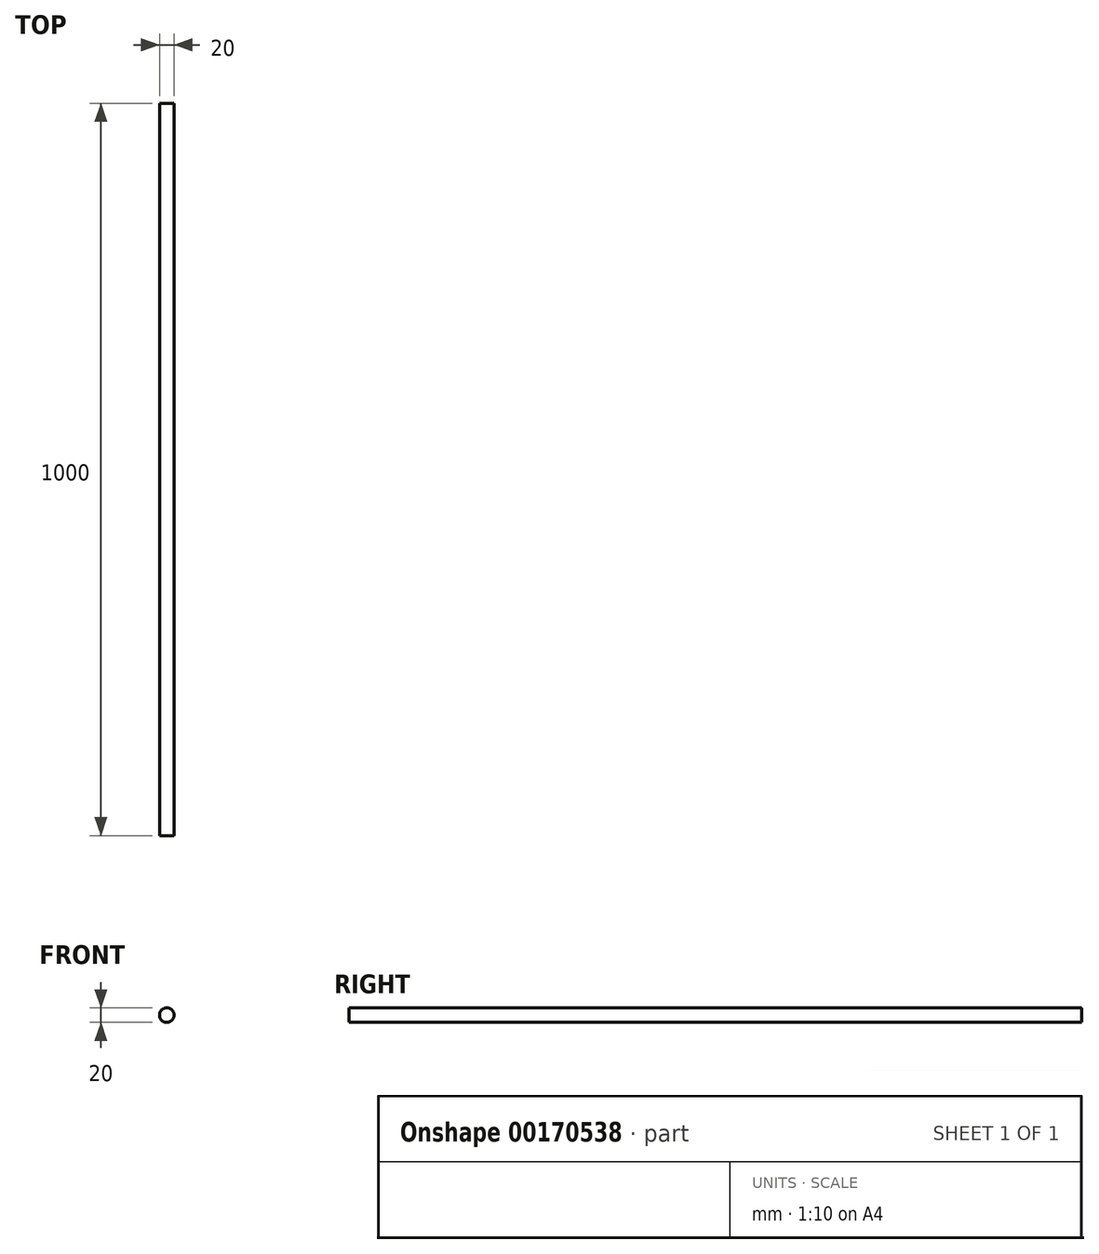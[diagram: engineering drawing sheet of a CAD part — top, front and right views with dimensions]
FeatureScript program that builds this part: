
annotation { "Feature Type Name" : "Feature", "Feature Type Description" : "" }
export const myFeature = defineFeature(function(context is Context, id is Id, definition is map)
    precondition{}
    {
        {
            var Q0;
            Q0=qCreatedBy(makeId("Front.planeOp"),FACE);
            var sketch = newSketch(context, id + "F0", { "sketchPlane" : qUnion([Q0])});
            skCircle(sketch, "E0", {"center": v(0, 0) * mm, "radius": 10 * mm});
            skSolve(sketch);
        }
        {
            var Q0;
            Q0 = qSketchRegion(id + "F0", true);
            extrude(context, id + "F1", {"entities" : qUnion([Q0]), "depth" : 200 * mm, "hasSecondDirection" : true, "secondDirectionOppositeDirection" : true, "secondDirectionDepth" : 800 * mm});
        }
    });
